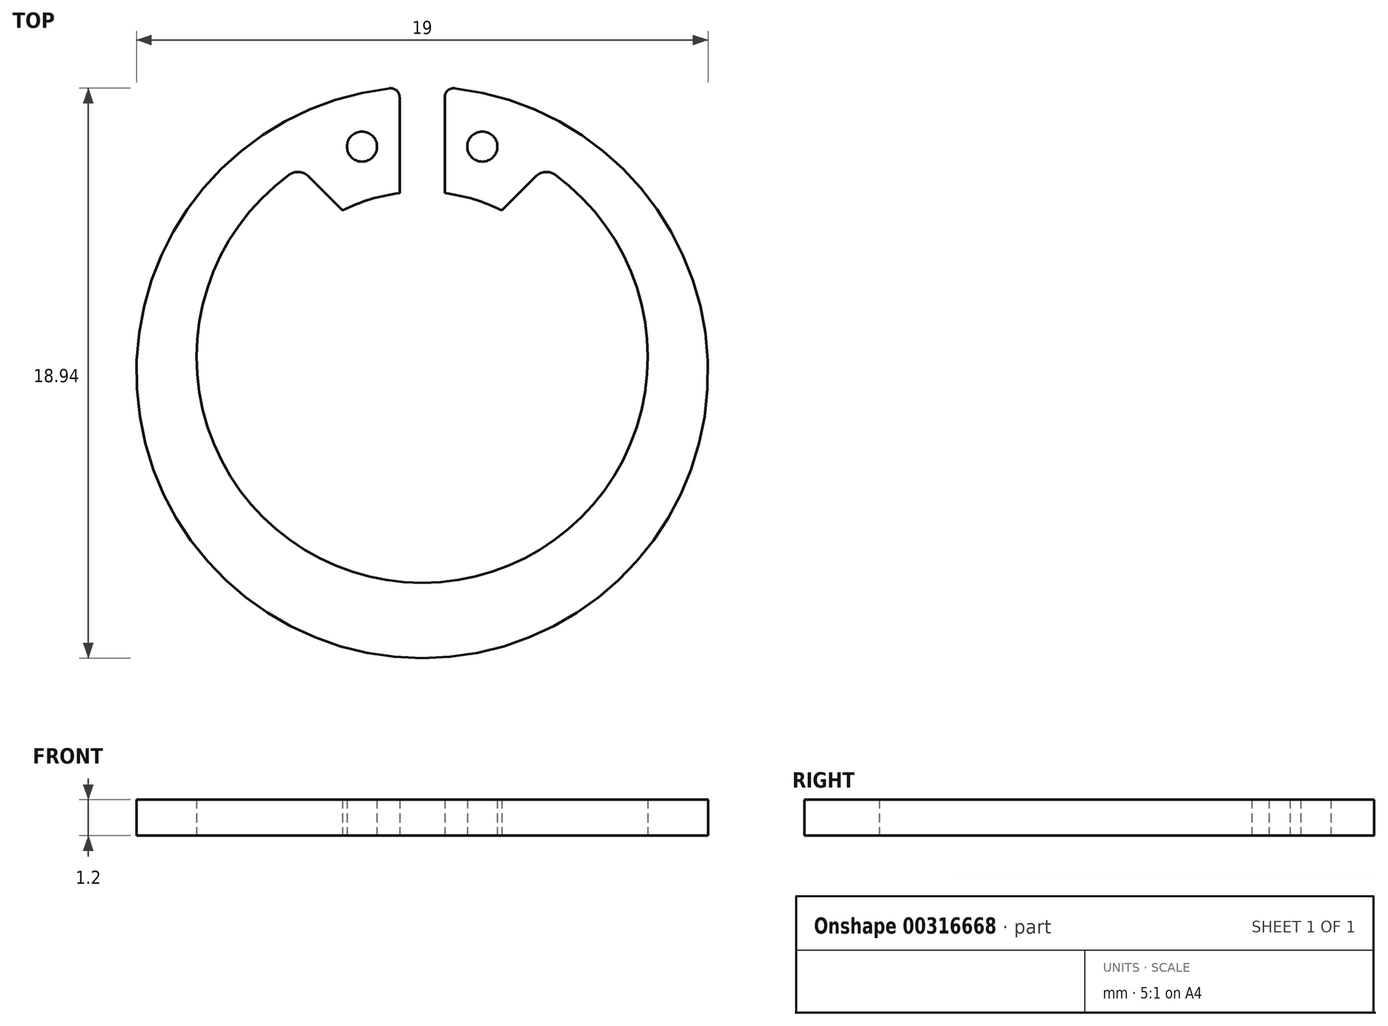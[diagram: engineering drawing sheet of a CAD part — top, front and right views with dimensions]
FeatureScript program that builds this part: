
annotation { "Feature Type Name" : "Feature", "Feature Type Description" : "" }
export const myFeature = defineFeature(function(context is Context, id is Id, definition is map)
    precondition{}
    {
        {
            var Q0;
            Q0=qCreatedBy(makeId("Top.planeOp"),FACE);
            var sketch = newSketch(context, id + "F0", { "sketchPlane" : qUnion([Q0])});
            skCircle(sketch, "E0", {"center": v(0, 0) * mm, "radius": 9.5 * mm});
            skCircle(sketch, "E1", {"center": v(0, 0.5) * mm, "radius": 7.5 * mm});
            skCircle(sketch, "E2", {"center": v(0, 0) * mm, "radius": 6 * mm});
            skLineSegment(sketch, "E3", {"start": v(-0.75, 9.47) * mm, "end": v(-0.75, 5.95) * mm});
            skCircle(sketch, "E4", {"center": v(-2, 7.5) * mm, "radius": 0.5 * mm});
            skLineSegment(sketch, "E5", {"start": v(-2.65, 5.38) * mm, "end": v(-4.07, 6.8) * mm});
            skLineSegment(sketch, "E6.MirrorCS", {"start": v(0.75, 9.47) * mm, "end": v(0.75, 5.95) * mm});
            skCircle(sketch, "E7.MirrorC", {"center": v(2, 7.5) * mm, "radius": 0.5 * mm});
            skLineSegment(sketch, "E8.MirrorCS", {"start": v(2.65, 5.38) * mm, "end": v(4.07, 6.8) * mm});
            skSolve(sketch);
        }
        {
            var Q0;
            {var subQ7=sQuery(id+"F0.wireOp",EDGE,"E3");var subQ11=sQuery(id+"F0.wireOp",EDGE,"E0");var subQ12=makeQuery(id+"F0.imprint","INTERSECT",VERTEX,{"derivedFrom":[subQ11,subQ7]});Q0=makeQuery(id+"F0.imprint","IMPRINT",FACE,{"disambiguationData":[TD([[makeQuery(id+"F0.imprint","IMPRINT",EDGE,{"disambiguationData":[TD([[subQ12,-1.0]])],"derivedFrom":subQ11}),1.0]])]});}
            var Q1;
            {var subQ5=sQuery(id+"F0.wireOp",EDGE,"E5");Q1=makeQuery(id+"F0.imprint","IMPRINT",FACE,{"disambiguationData":[TD([[makeQuery(id+"F0.imprint","IMPRINT",EDGE,{"derivedFrom":subQ5}),-1.0]])]});}
            var Q2;
            {var subQ5=sQuery(id+"F0.wireOp",EDGE,"E8.MirrorCS");Q2=makeQuery(id+"F0.imprint","IMPRINT",FACE,{"disambiguationData":[TD([[makeQuery(id+"F0.imprint","IMPRINT",EDGE,{"derivedFrom":subQ5}),1.0]])]});}
            var Q3;
            Q3=sQuery(id+"F0.wireOp",EDGE,"E0");
            var Q4;
            Q4=sQuery(id+"F0.wireOp",EDGE,"E3");
            var Q5;
            Q5=sQuery(id+"F0.wireOp",EDGE,"E5");
            var Q6;
            Q6=sQuery(id+"F0.wireOp",EDGE,"E2");
            var Q7;
            Q7=sQuery(id+"F0.wireOp",EDGE,"E1");
            var Q8;
            Q8=sQuery(id+"F0.wireOp",EDGE,"E4");
            extrude(context, id + "F1", {"entities" : qUnion([Q0, Q1, Q2]), "surfaceEntities" : qUnion([Q3, Q4, Q5, Q6, Q7, Q8]), "depth" : 1.2 * mm});
        }
        {
            var Q0;
            Q0=makeQuery(id+"F1.opExtrude","SWEPT_EDGE",EDGE,{"disambiguationData":[OSD([sQuery(id+"F0.wireOp",EDGE,"E0"),sQuery(id+"F0.wireOp",EDGE,"E3")])]});
            var Q1;
            Q1=makeQuery(id+"F1.opExtrude","SWEPT_EDGE",EDGE,{"disambiguationData":[OSD([sQuery(id+"F0.wireOp",EDGE,"E0"),sQuery(id+"F0.wireOp",EDGE,"E6.MirrorCS")])]});
            fillet(context, id + "F2", {"entities" : qUnion([Q0, Q1]), "radius" : 0.3 * mm, "tangentPropagation" : true, "allowEdgeOverflow" : false});
        }
        {
            var Q0;
            Q0=makeQuery(id+"F1.opExtrude","SWEPT_EDGE",EDGE,{"disambiguationData":[OSD([sQuery(id+"F0.wireOp",EDGE,"E1"),sQuery(id+"F0.wireOp",EDGE,"E5")])]});
            var Q1;
            Q1=makeQuery(id+"F1.opExtrude","SWEPT_EDGE",EDGE,{"disambiguationData":[OSD([sQuery(id+"F0.wireOp",EDGE,"E1"),sQuery(id+"F0.wireOp",EDGE,"E8.MirrorCS")])]});
            fillet(context, id + "F3", {"entities" : qUnion([Q0, Q1]), "radius" : 0.5 * mm, "tangentPropagation" : true, "allowEdgeOverflow" : false});
        }
    });
